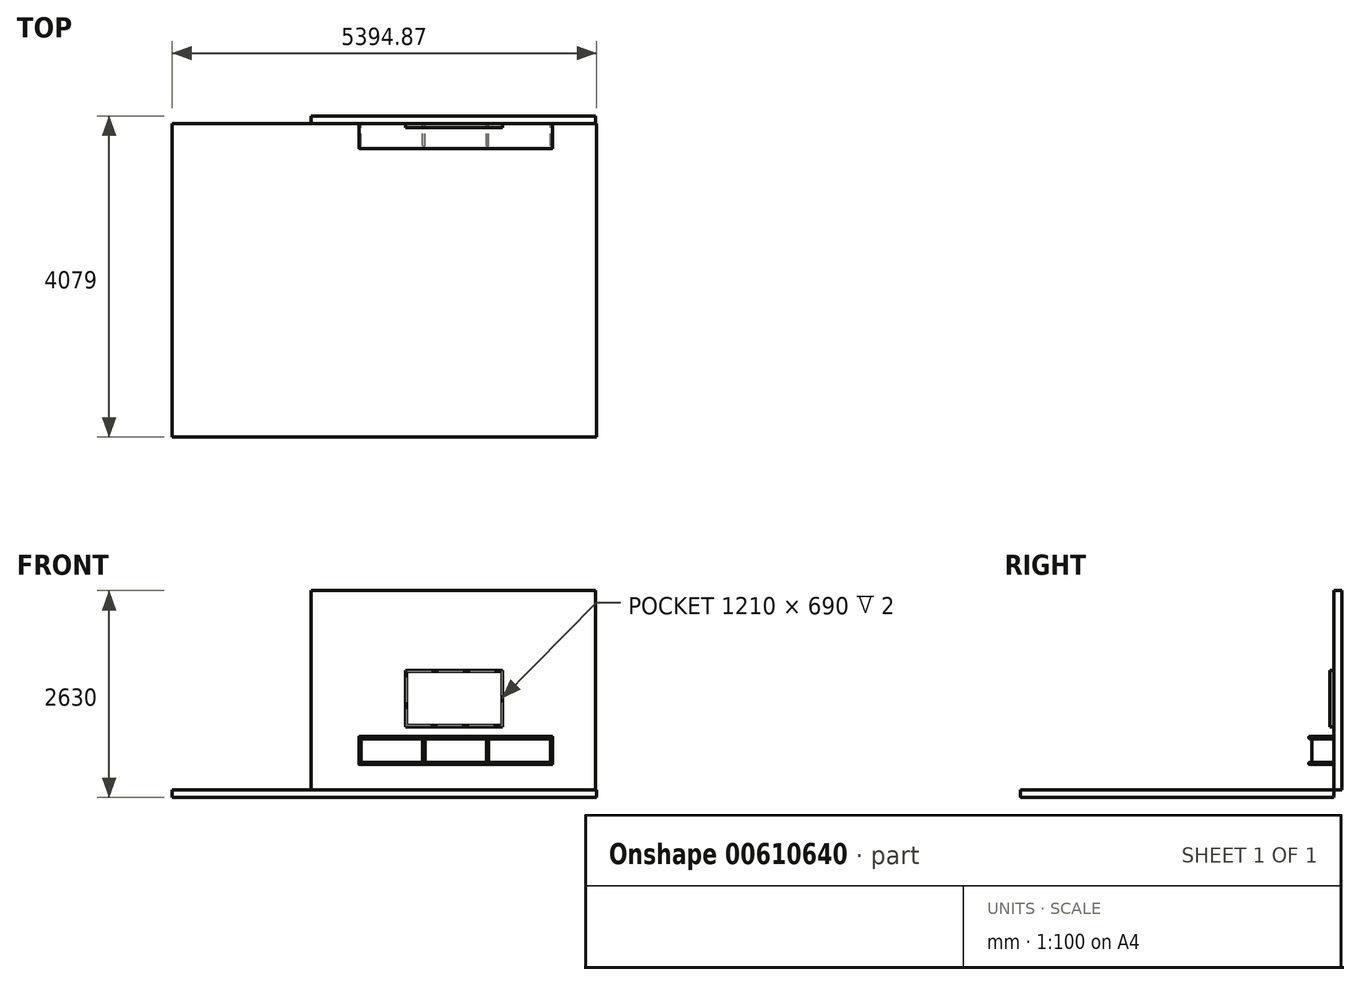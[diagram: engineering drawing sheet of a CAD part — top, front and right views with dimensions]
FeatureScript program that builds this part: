
annotation { "Feature Type Name" : "Feature", "Feature Type Description" : "" }
export const myFeature = defineFeature(function(context is Context, id is Id, definition is map)
    precondition{}
    {
        {
            var Q0;
            Q0=qCreatedBy(makeId("Front.planeOp"),FACE);
            var sketch = newSketch(context, id + "F0", { "sketchPlane" : qUnion([Q0])});
            skLineSegment(sketch, "E0.bottom", {"start": v(-1805, 0) * mm, "end": v(1805, 0) * mm});
            skLineSegment(sketch, "E0.top", {"start": v(-1805, 2530) * mm, "end": v(1805, 2530) * mm});
            skLineSegment(sketch, "E0.left", {"start": v(-1805, 0) * mm, "end": v(-1805, 2530) * mm});
            skLineSegment(sketch, "E0.right", {"start": v(1805, 0) * mm, "end": v(1805, 2530) * mm});
            skPoint(sketch, "E1", {"position": v(0, 0) * mm});
            skSolve(sketch);
        }
        {
            var Q0;
            Q0=makeQuery(id+"F0.imprint","IMPRINT",FACE,{"disambiguationData":[TD([[makeQuery(id+"F0.imprint","IMPRINT",EDGE,{"derivedFrom":sQuery(id+"F0.wireOp",EDGE,"E0.bottom")}),1.0]])]});
            extrude(context, id + "F1", {"entities" : qUnion([Q0]), "oppositeDirection" : true, "depth" : 100 * mm, "offsetDistance" : 25 * mm});
        }
        {
            var Q0;
            Q0=qCreatedBy(makeId("Top.planeOp"),FACE);
            var sketch = newSketch(context, id + "F2", { "sketchPlane" : qUnion([Q0])});
            skLineSegment(sketch, "E2.bottom", {"start": v(1820.18, 0) * mm, "end": v(-3574.69, 0) * mm});
            skLineSegment(sketch, "E2.top", {"start": v(1820.18, -3979) * mm, "end": v(-3574.69, -3979) * mm});
            skLineSegment(sketch, "E2.left", {"start": v(1820.18, 0) * mm, "end": v(1820.18, -3979) * mm});
            skLineSegment(sketch, "E2.right", {"start": v(-3574.69, 0) * mm, "end": v(-3574.69, -3979) * mm});
            skSolve(sketch);
        }
        {
            var Q0;
            Q0=qSketchRegion(id+"F2",true);
            extrude(context, id + "F3", {"entities" : qUnion([Q0]), "operationType" : NewBodyOperationType.ADD, "oppositeDirection" : true, "depth" : 100 * mm, "offsetDistance" : 25 * mm});
        }
        {
            var Q0;
            Q0=makeQuery(id+"F1.opExtrude","CAP_FACE",FACE,{"disambiguationData":[OSD([sQuery(id+"F0.wireOp",EDGE,"E0.bottom"),sQuery(id+"F0.wireOp",EDGE,"E0.top"),sQuery(id+"F0.wireOp",EDGE,"E0.left"),sQuery(id+"F0.wireOp",EDGE,"E0.right")])],"isStart":true});
            var sketch = newSketch(context, id + "F4", { "sketchPlane" : qUnion([Q0])});
            skLineSegment(sketch, "E3.bottom", {"start": v(625, 800) * mm, "end": v(-605, 800) * mm});
            skLineSegment(sketch, "E3.top", {"start": v(625, 1515) * mm, "end": v(-605, 1515) * mm});
            skLineSegment(sketch, "E3.left", {"start": v(625, 800) * mm, "end": v(625, 1515) * mm});
            skLineSegment(sketch, "E3.right", {"start": v(-605, 800) * mm, "end": v(-605, 1515) * mm});
            skPoint(sketch, "E3.middle", {"position": v(10, 1157.5) * mm});
            skSolve(sketch);
        }
        {
            var Q0;
            Q0=qSketchRegion(id+"F4",true);
            extrude(context, id + "F5", {"entities" : qUnion([Q0]), "depth" : 50 * mm, "offsetDistance" : 25 * mm});
        }
        {
            var Q0;
            Q0=makeQuery(id+"F5.opExtrude","CAP_FACE",FACE,{"disambiguationData":[OSD([sQuery(id+"F4.wireOp",EDGE,"E3.bottom"),sQuery(id+"F4.wireOp",EDGE,"E3.top"),sQuery(id+"F4.wireOp",EDGE,"E3.left"),sQuery(id+"F4.wireOp",EDGE,"E3.right")])],"isStart":false});
            var sketch = newSketch(context, id + "F6", { "sketchPlane" : qUnion([Q0])});
            skLineSegment(sketch, "E4.bottom", {"start": v(-595, 1505) * mm, "end": v(615, 1505) * mm});
            skLineSegment(sketch, "E4.top", {"start": v(-595, 815) * mm, "end": v(615, 815) * mm});
            skLineSegment(sketch, "E4.left", {"start": v(-595, 1505) * mm, "end": v(-595, 815) * mm});
            skLineSegment(sketch, "E4.right", {"start": v(615, 1505) * mm, "end": v(615, 815) * mm});
            skSolve(sketch);
        }
        {
            var Q0;
            Q0=qSketchRegion(id+"F6",true);
            extrude(context, id + "F7", {"entities" : qUnion([Q0]), "operationType" : NewBodyOperationType.REMOVE, "oppositeDirection" : true, "depth" : 2 * mm, "offsetDistance" : 25 * mm});
        }
        {
            var Q0;
            Q0=makeQuery(id+"F1.opExtrude","CAP_FACE",FACE,{"disambiguationData":[OSD([sQuery(id+"F0.wireOp",EDGE,"E0.bottom"),sQuery(id+"F0.wireOp",EDGE,"E0.top"),sQuery(id+"F0.wireOp",EDGE,"E0.left"),sQuery(id+"F0.wireOp",EDGE,"E0.right")])],"isStart":true});
            var sketch = newSketch(context, id + "F8", { "sketchPlane" : qUnion([Q0])});
            skLineSegment(sketch, "E5.bottom", {"start": v(-1200.26, 676) * mm, "end": v(1259.74, 676) * mm});
            skLineSegment(sketch, "E5.top", {"start": v(-1200.26, 648) * mm, "end": v(1259.74, 648) * mm});
            skLineSegment(sketch, "E5.left", {"start": v(-1200.26, 676) * mm, "end": v(-1200.26, 648) * mm});
            skLineSegment(sketch, "E5.right", {"start": v(1259.74, 676) * mm, "end": v(1259.74, 648) * mm});
            skLineSegment(sketch, "E6.bottom", {"start": v(-1200.26, 348) * mm, "end": v(1259.74, 348) * mm});
            skLineSegment(sketch, "E6.top", {"start": v(-1200.26, 320) * mm, "end": v(1259.74, 320) * mm});
            skLineSegment(sketch, "E6.left", {"start": v(-1200.26, 348) * mm, "end": v(-1200.26, 320) * mm});
            skLineSegment(sketch, "E6.right", {"start": v(1259.74, 348) * mm, "end": v(1259.74, 320) * mm});
            skSolve(sketch);
        }
        {
            var Q0;
            Q0=qSketchRegion(id+"F8",true);
            extrude(context, id + "F9", {"entities" : qUnion([Q0]), "depth" : 315 * mm, "offsetDistance" : 25 * mm});
        }
        {
            var Q0;
            Q0=makeQuery(id+"F1.opExtrude","CAP_FACE",FACE,{"disambiguationData":[OSD([sQuery(id+"F0.wireOp",EDGE,"E0.bottom"),sQuery(id+"F0.wireOp",EDGE,"E0.top"),sQuery(id+"F0.wireOp",EDGE,"E0.left"),sQuery(id+"F0.wireOp",EDGE,"E0.right")])],"isStart":true});
            var sketch = newSketch(context, id + "F10", { "sketchPlane" : qUnion([Q0])});
            skLineSegment(sketch, "E7.bottom", {"start": v(-1200.26, 348) * mm, "end": v(-1172.26, 348) * mm});
            skLineSegment(sketch, "E7.top", {"start": v(-1200.26, 648) * mm, "end": v(-1172.26, 648) * mm});
            skLineSegment(sketch, "E7.left", {"start": v(-1200.26, 348) * mm, "end": v(-1200.26, 648) * mm});
            skLineSegment(sketch, "E7.right", {"start": v(-1172.26, 348) * mm, "end": v(-1172.26, 648) * mm});
            skLineSegment(sketch, "E8.bottom", {"start": v(1231.74, 348) * mm, "end": v(1259.74, 348) * mm});
            skLineSegment(sketch, "E8.top", {"start": v(1231.74, 648) * mm, "end": v(1259.74, 648) * mm});
            skLineSegment(sketch, "E8.left", {"start": v(1231.74, 348) * mm, "end": v(1231.74, 648) * mm});
            skLineSegment(sketch, "E8.right", {"start": v(1259.74, 348) * mm, "end": v(1259.74, 648) * mm});
            skLineSegment(sketch, "E9.bottom", {"start": v(-389.59, 348) * mm, "end": v(-361.59, 348) * mm});
            skLineSegment(sketch, "E9.top", {"start": v(-389.59, 648) * mm, "end": v(-361.59, 648) * mm});
            skLineSegment(sketch, "E9.left", {"start": v(-389.59, 348) * mm, "end": v(-389.59, 648) * mm});
            skLineSegment(sketch, "E9.right", {"start": v(-361.59, 348) * mm, "end": v(-361.59, 648) * mm});
            skLineSegment(sketch, "E10.bottom", {"start": v(421.08, 648) * mm, "end": v(449.08, 648) * mm});
            skLineSegment(sketch, "E10.top", {"start": v(421.08, 348) * mm, "end": v(449.08, 348) * mm});
            skLineSegment(sketch, "E10.left", {"start": v(421.08, 648) * mm, "end": v(421.08, 348) * mm});
            skLineSegment(sketch, "E10.right", {"start": v(449.08, 648) * mm, "end": v(449.08, 348) * mm});
            skSolve(sketch);
        }
        {
            var Q0;
            Q0=qSketchRegion(id+"F10",true);
            extrude(context, id + "F11", {"entities" : qUnion([Q0]), "depth" : 280 * mm, "offsetDistance" : 25 * mm});
        }
        {
            var Q0;
            Q0=makeQuery(id+"F9.opExtrude","CAP_EDGE",EDGE,{"disambiguationData":[OSD([sQuery(id+"F8.wireOp",EDGE,"E5.left")])],"isStart":false});
            var Q1;
            Q1=makeQuery(id+"F9.opExtrude","SWEPT_EDGE",EDGE,{"disambiguationData":[OSD([sQuery(id+"F8.wireOp",EDGE,"E5.bottom"),sQuery(id+"F8.wireOp",EDGE,"E5.left")])]});
            var Q2;
            Q2=makeQuery(id+"F9.opExtrude","SWEPT_EDGE",EDGE,{"disambiguationData":[OSD([sQuery(id+"F8.wireOp",EDGE,"E5.top"),sQuery(id+"F8.wireOp",EDGE,"E5.left")])]});
            var Q3;
            Q3=makeQuery(id+"F9.opExtrude","CAP_EDGE",EDGE,{"disambiguationData":[OSD([sQuery(id+"F8.wireOp",EDGE,"E5.top")])],"isStart":false});
            var Q4;
            Q4=makeQuery(id+"F9.opExtrude","CAP_EDGE",EDGE,{"disambiguationData":[OSD([sQuery(id+"F8.wireOp",EDGE,"E5.bottom")])],"isStart":false});
            var Q5;
            Q5=makeQuery(id+"F9.opExtrude","SWEPT_EDGE",EDGE,{"disambiguationData":[OSD([sQuery(id+"F8.wireOp",EDGE,"E6.bottom"),sQuery(id+"F8.wireOp",EDGE,"E6.left")])]});
            var Q6;
            Q6=makeQuery(id+"F9.opExtrude","SWEPT_EDGE",EDGE,{"disambiguationData":[OSD([sQuery(id+"F8.wireOp",EDGE,"E6.top"),sQuery(id+"F8.wireOp",EDGE,"E6.left")])]});
            var Q7;
            Q7=makeQuery(id+"F9.opExtrude","CAP_EDGE",EDGE,{"disambiguationData":[OSD([sQuery(id+"F8.wireOp",EDGE,"E6.left")])],"isStart":false});
            var Q8;
            Q8=makeQuery(id+"F9.opExtrude","CAP_EDGE",EDGE,{"disambiguationData":[OSD([sQuery(id+"F8.wireOp",EDGE,"E6.top")])],"isStart":false});
            var Q9;
            Q9=makeQuery(id+"F9.opExtrude","SWEPT_EDGE",EDGE,{"disambiguationData":[OSD([sQuery(id+"F8.wireOp",EDGE,"E5.bottom"),sQuery(id+"F8.wireOp",EDGE,"E5.right")])]});
            var Q10;
            Q10=makeQuery(id+"F9.opExtrude","CAP_EDGE",EDGE,{"disambiguationData":[OSD([sQuery(id+"F8.wireOp",EDGE,"E6.right")])],"isStart":false});
            var Q11;
            Q11=makeQuery(id+"F9.opExtrude","SWEPT_EDGE",EDGE,{"disambiguationData":[OSD([sQuery(id+"F8.wireOp",EDGE,"E6.top"),sQuery(id+"F8.wireOp",EDGE,"E6.right")])]});
            var Q12;
            Q12=makeQuery(id+"F9.opExtrude","SWEPT_EDGE",EDGE,{"disambiguationData":[OSD([sQuery(id+"F8.wireOp",EDGE,"E6.bottom"),sQuery(id+"F8.wireOp",EDGE,"E6.right")])]});
            var Q13;
            Q13=makeQuery(id+"F9.opExtrude","SWEPT_EDGE",EDGE,{"disambiguationData":[OSD([sQuery(id+"F8.wireOp",EDGE,"E5.top"),sQuery(id+"F8.wireOp",EDGE,"E5.right")])]});
            var Q14;
            Q14=makeQuery(id+"F9.opExtrude","CAP_EDGE",EDGE,{"disambiguationData":[OSD([sQuery(id+"F8.wireOp",EDGE,"E5.right")])],"isStart":false});
            var Q15;
            Q15=makeQuery(id+"F9.opExtrude","CAP_EDGE",EDGE,{"disambiguationData":[OSD([sQuery(id+"F8.wireOp",EDGE,"E6.bottom")])],"isStart":false});
            fillet(context, id + "F12", {"entities" : qUnion([Q0, Q1, Q2, Q3, Q4, Q5, Q6, Q7, Q8, Q9, Q10, Q11, Q12, Q13, Q14, Q15]), "radius" : 5 * mm, "tangentPropagation" : true, "allowEdgeOverflow" : false});
        }
        {
            var Q0;
            Q0=makeQuery(id+"F11.opExtrude","CAP_EDGE",EDGE,{"disambiguationData":[OSD([sQuery(id+"F10.wireOp",EDGE,"E7.left")])],"isStart":false});
            var Q1;
            Q1=makeQuery(id+"F11.opExtrude","CAP_EDGE",EDGE,{"disambiguationData":[OSD([sQuery(id+"F10.wireOp",EDGE,"E9.left")])],"isStart":false});
            var Q2;
            Q2=makeQuery(id+"F11.opExtrude","CAP_EDGE",EDGE,{"disambiguationData":[OSD([sQuery(id+"F10.wireOp",EDGE,"E8.left")])],"isStart":false});
            var Q3;
            Q3=makeQuery(id+"F11.opExtrude","CAP_EDGE",EDGE,{"disambiguationData":[OSD([sQuery(id+"F10.wireOp",EDGE,"E7.right")])],"isStart":false});
            var Q4;
            Q4=makeQuery(id+"F11.opExtrude","CAP_EDGE",EDGE,{"disambiguationData":[OSD([sQuery(id+"F10.wireOp",EDGE,"E9.right")])],"isStart":false});
            var Q5;
            Q5=makeQuery(id+"F11.opExtrude","CAP_EDGE",EDGE,{"disambiguationData":[OSD([sQuery(id+"F10.wireOp",EDGE,"E8.right")])],"isStart":false});
            var Q6;
            Q6=makeQuery(id+"F11.opExtrude","CAP_EDGE",EDGE,{"disambiguationData":[OSD([sQuery(id+"F10.wireOp",EDGE,"E10.left")])],"isStart":false});
            var Q7;
            Q7=makeQuery(id+"F11.opExtrude","CAP_EDGE",EDGE,{"disambiguationData":[OSD([sQuery(id+"F10.wireOp",EDGE,"E10.right")])],"isStart":false});
            fillet(context, id + "F13", {"entities" : qUnion([Q0, Q1, Q2, Q3, Q4, Q5, Q6, Q7]), "radius" : 5 * mm, "tangentPropagation" : true, "allowEdgeOverflow" : false});
        }
    });
